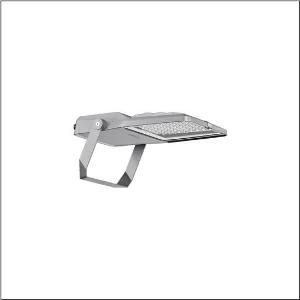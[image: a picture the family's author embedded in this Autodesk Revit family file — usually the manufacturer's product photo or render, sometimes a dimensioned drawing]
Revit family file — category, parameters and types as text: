
# Revit family: floodlight_fl_21_iq_mini___rs12_5xa7772c5b1a_b916
name_source: partatom
category: Lighting Fixtures
units: mm (PartAtom-declared; Revit-internal decimal feet)

## family parameters
Cut with Voids When Loaded = No
Host = Face
Light Source = No
Part Type = Normal
Room Calculation Point = No
Round Connector Dimension = Use Diameter
Shared = No

## types (1)
- --- (1 x LED, 11510 lm, 87.2 W, 4000K)
    Apparent Load = 87 VA
    CIE Flux Codes = 79 92 99 100 100
    Color Rendering = 80
    Color Temperature = 4000K
    Default Elevation = 1800 mm
    Description = Floodlight FL 21 iQ mini, floodlight, primary light control with lens, of PMMA, primary optical cover: protective disc, of toughened safety glass, transparent, light distribution: RS12, light emission: direct distribution, installation type: surface-mounted, lamps: LED, High Power LED, rated values: 11.510lm | 87,2W | 132lm/W (begin service life); end service life: 11.510lm | 92,1W; at 50% lumin. flux: 5.755lm | 40,1W | 143,5lm/W, colour temperature: 4000K, colour rendering: CRI > 80, light colour: 840, light setting 1 begin service life: 100% | 11.510lm | 87,2W | 132lm/W | 4.000K, light setting 1 end service life: 92,1W, further light settings possible, control: Street-Remote, Auto-Match, Temp-Guard, Night-Set, Smart-Wire, Desk-Remote (wireless, voltage-free reading and setting of iQ features in the workshop via application-optimized NFC function/RFID function), optimised constant luminous flux control (CLO 2.0), pre-setting: linear dimming characteristic, with terminal, 6-pole, mains connection: 220..240V, AC, 50/60Hz, luminaire housing, of diecast aluminium, powder-coated, SITECO metallic grey (DB 702S), corrosivity category C5 mid according to DIN EN ISO 12944suitable for swimming poolschlorine-resistant, sealing non-destructively replaceable, mounting bracket, of steel, galvanised, powder-coated, SITECO metallic grey (DB 702S), protection rating (complete): IP66, insulation class (complete): insulation class II (safety insulation), certification: CE, ENEC, VDE, protection symbol: D, impact resistance: IK08, permissible operating ambient temperature: -40..+40°C, permissible operating ambient temperature for outdoor applications: -40..+50°C, standard: DIN EN 12944, LABS conformity tested according to VDMA 24364:2018-05, packaging unit: 1 piece

Light Distribution: RS12
    Height = 70 mm
    Lamp = 1 x LED
    Lamp Light Flux = 11510 lm
    Lamp Power = 87.2 W
    Lamp count = 1
    Length = 485 mm
    Luminous efficacy = 132 lm/W
    Manufacturer = Siteco
    ModVariant = No
    Model = 5XA7772C5B1A
    Mounting Place = Pole
    Mounting Type = Pole annexe
    Number of Poles = 1
    OnlyDefault = Yes
    Power Factor = 1
    Product Name = Floodlight FL 21 iQ mini | RS12
    Product group = floodlight | pylon annexe
    ProductGroupID = 6201
    Protection Class = Protection class II
    Protection Degree = IP 66
    RLX_Detail_Level = 1
    RLX_Emergency_Light_Flux = 0 lm
    RLX_Emergency_Type = 0
    RLX_Emergency_Type_DB = No
    RlxData = <blob elided: 91297 chars, md5=32a7229e>
    Socket = socket
    Standby Power = 0 W
    System Light Flux = 11510 lm
    System Power = 87 W
    Type Comments = factory setting: luminous flux: 100 % | dim-lin: 254 | 456 mA
    Type Image = l_1006845.jpg
    URL = http://relux.com
    VarID = @adj_168561
    Voltage = 0 V
    Weight = 0.00 kg
    Width = 337 mm

## geometry (parser evidence)
native form markers: Blend x4, Sweep x14
no freeform markers — native parametric forms only
